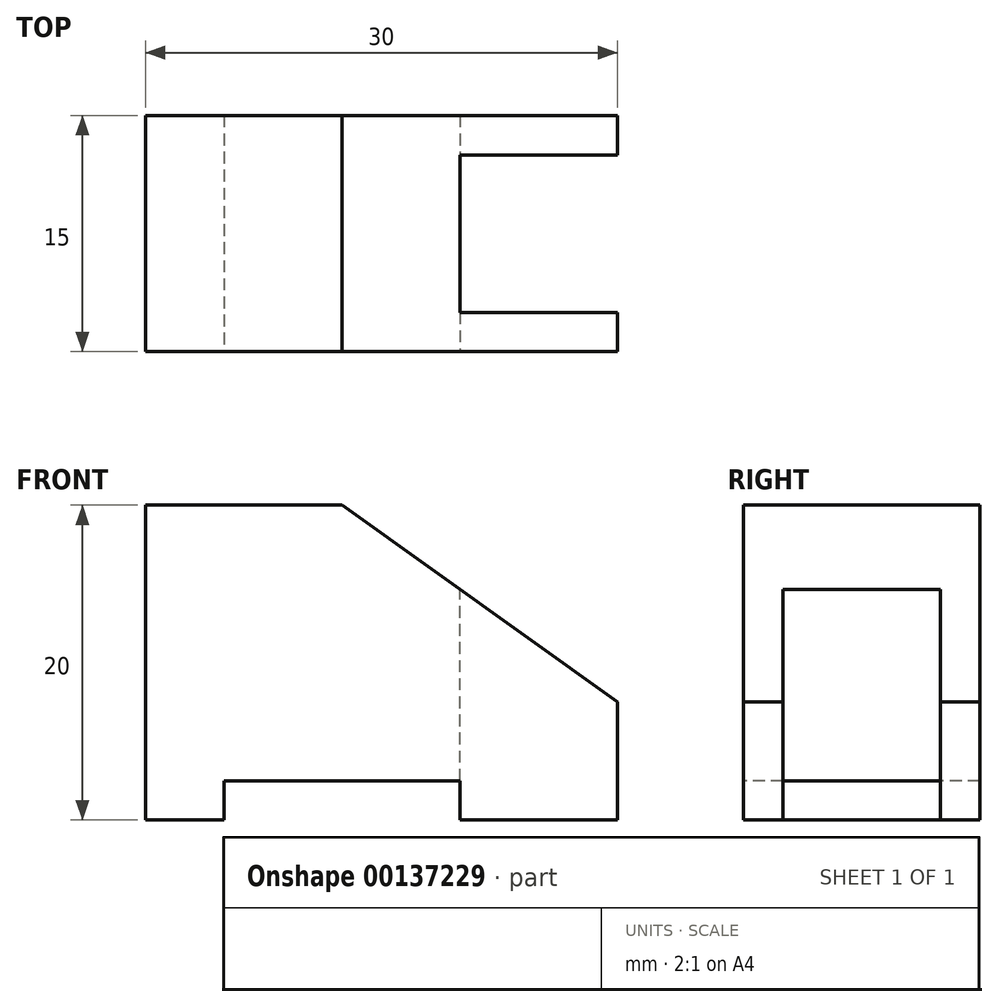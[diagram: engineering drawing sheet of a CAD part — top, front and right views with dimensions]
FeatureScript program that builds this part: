
annotation { "Feature Type Name" : "Feature", "Feature Type Description" : "" }
export const myFeature = defineFeature(function(context is Context, id is Id, definition is map)
    precondition{}
    {
        {
            var Q0;
            Q0=qCreatedBy(makeId("Front.planeOp"),FACE);
            var sketch = newSketch(context, id + "F0", { "sketchPlane" : qUnion([Q0])});
            skLineSegment(sketch, "E0", {"start": v(0, 0) * mm, "end": v(5, 0) * mm});
            skLineSegment(sketch, "E1", {"start": v(5, 0) * mm, "end": v(5, 2.5) * mm});
            skLineSegment(sketch, "E2", {"start": v(5, 2.5) * mm, "end": v(20, 2.5) * mm});
            skLineSegment(sketch, "E3", {"start": v(20, 2.5) * mm, "end": v(20, 0) * mm});
            skLineSegment(sketch, "E4", {"start": v(20, 0) * mm, "end": v(30, 0) * mm});
            skLineSegment(sketch, "E5", {"start": v(0, 0) * mm, "end": v(0, 20) * mm});
            skLineSegment(sketch, "E6", {"start": v(0, 20) * mm, "end": v(12.5, 20) * mm});
            skLineSegment(sketch, "E7", {"start": v(12.5, 20) * mm, "end": v(30, 7.5) * mm});
            skLineSegment(sketch, "E8", {"start": v(30, 7.5) * mm, "end": v(30, 0) * mm});
            skSolve(sketch);
        }
        {
            var Q0;
            Q0=makeQuery(id+"F0.imprint","IMPRINT",FACE,{"disambiguationData":[TD([[makeQuery(id+"F0.imprint","IMPRINT",EDGE,{"derivedFrom":sQuery(id+"F0.wireOp",EDGE,"E0")}),1.0]])]});
            extrude(context, id + "F1", {"entities" : qUnion([Q0]), "oppositeDirection" : true, "depth" : 15 * mm});
        }
        {
            var Q0;
            Q0=makeQuery(id+"F1.opExtrude","SWEPT_FACE",FACE,{"disambiguationData":[OSD([sQuery(id+"F0.wireOp",EDGE,"E8")])]});
            var sketch = newSketch(context, id + "F2", { "sketchPlane" : qUnion([Q0])});
            skLineSegment(sketch, "E9", {"start": v(0, 0) * mm, "end": v(2.5, 0) * mm, "construction": true});
            skLineSegment(sketch, "E10", {"start": v(2.5, 0) * mm, "end": v(2.5, 15) * mm});
            skLineSegment(sketch, "E11", {"start": v(2.5, 15) * mm, "end": v(12.5, 15) * mm});
            skLineSegment(sketch, "E12", {"start": v(12.5, 15) * mm, "end": v(12.5, 0) * mm});
            skLineSegment(sketch, "E13", {"start": v(12.5, 0) * mm, "end": v(15, 0) * mm, "construction": true});
            skSolve(sketch);
        }
        {
            var Q0;
            {var subQ0=sQuery(id+"F2.wireOp",EDGE,"E11");Q0=makeQuery(id+"F2.imprint","IMPRINT",FACE,{"disambiguationData":[TD([[makeQuery(id+"F2.imprint","IMPRINT",EDGE,{"derivedFrom":subQ0}),-1.0]])]});}
            var Q1;
            {var subQ0=sQuery(id+"F2.wireOp",EDGE,"E10");var subQ1=sQuery(id+"F0.wireOp",EDGE,"E8");var subQ2=makeQuery(id+"F1.opExtrude","SWEPT_EDGE",EDGE,{"disambiguationData":[OSD([sQuery(id+"F0.wireOp",EDGE,"E4"),subQ1])]});var subQ3=makeQuery(id+"F2.imprint","INTERSECT",VERTEX,{"derivedFrom":[subQ2,subQ0]});Q1=makeQuery(id+"F2.imprint","IMPRINT",FACE,{"disambiguationData":[TD([[makeQuery(id+"F2.imprint","IMPRINT",EDGE,{"disambiguationData":[TD([[subQ3,-1.0]])],"derivedFrom":subQ0}),-1.0]])]});}
            extrude(context, id + "F3", {"entities" : qUnion([Q0, Q1]), "operationType" : NewBodyOperationType.REMOVE, "oppositeDirection" : true, "depth" : 10 * mm});
        }
    });
